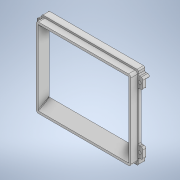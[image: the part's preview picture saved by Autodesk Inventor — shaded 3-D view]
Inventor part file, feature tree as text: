
AUTODESK INVENTOR PART (.ipt)
format: ipt  version: 2020 (Build 240168000, 168)  size: 298,496 bytes
history: native  units: mm
features: sketch x6, extrude x5, fillet x4, chamfer x2, hole x1, projected_geometry x1
ambient origin geometry x8: Origin, YZ Plane, XZ Plane, XY Plane, X Axis, Y Axis, Z Axis, Center Point
bodies: Solid1 (feature_tree)
feature tree (19):
  extrude  "Extrusion1"  Depth=140.0mm
  extrude  "Extrusion2"  Depth=18.0mm
  extrude  "Extrusion3"  Depth=12.0mm
  chamfer  "Chamfer1"  Distance=5.0mm
  chamfer  "Chamfer2"  Distance=11.0mm
  fillet  "Fillet1"  Radius=99.5mm
  fillet  "Fillet3"  Radius=20.0mm
  fillet  "Fillet4"  Radius=22.68928mm
  fillet  "Fillet5"  Radius=22.68928mm
  hole  "Hole1"  [1 undecoded]
  extrude  "Extrusion4"  Depth=4.0mm
  extrude  "Extrusion5"  Depth=3.0mm
  sketch  "Sketch1"  dims[d0=163.0mm d1=140.0mm]
  sketch  "Sketch2"  dims[d2=8.0mm d3=18.0mm]
  sketch  "Sketch3"  dims[d4=8.0mm d5=12.0mm d6=5.0mm d7=0.0mm d10=11.0mm d11=0.0mm d12=99.5mm d13=20.0mm d14=22.68928mm d15=22.68928mm]
  sketch  "Sketch4"  dims[d16=148.0mm d17=0.0mm d18=2.82mm d19=2.0mm d20=13.962634mm]
  sketch  "Sketch5"  dims[d21=2.82mm d22=2.0mm d23=13.962634mm d24=4.0mm]
  projected_geometry  "Projected Loop1"
  sketch  "Sketch6"  dims[d26=1.0mm d27=3.0mm d28=2.0mm d30=168.0mm d31=5.2mm d32=7.4mm d33=4.0mm d34=2.0mm d35=90.0deg d36=11.9mm d37=20.594885mm d38=102.0mm d39=101.8mm d40=192.8mm d41=117.5mm d42=6.0mm d43=0.0mm d44=3.0mm d45=70.0mm d46=6.0mm d47=0.0mm d48=160.0mm d49=134.0mm d50=14.5mm]
note: 1 required parameter value undecoded (feature->parameter linkage not recoverable at this tier; creation-order binding heuristic only, values carry confidence <= 0.55)
